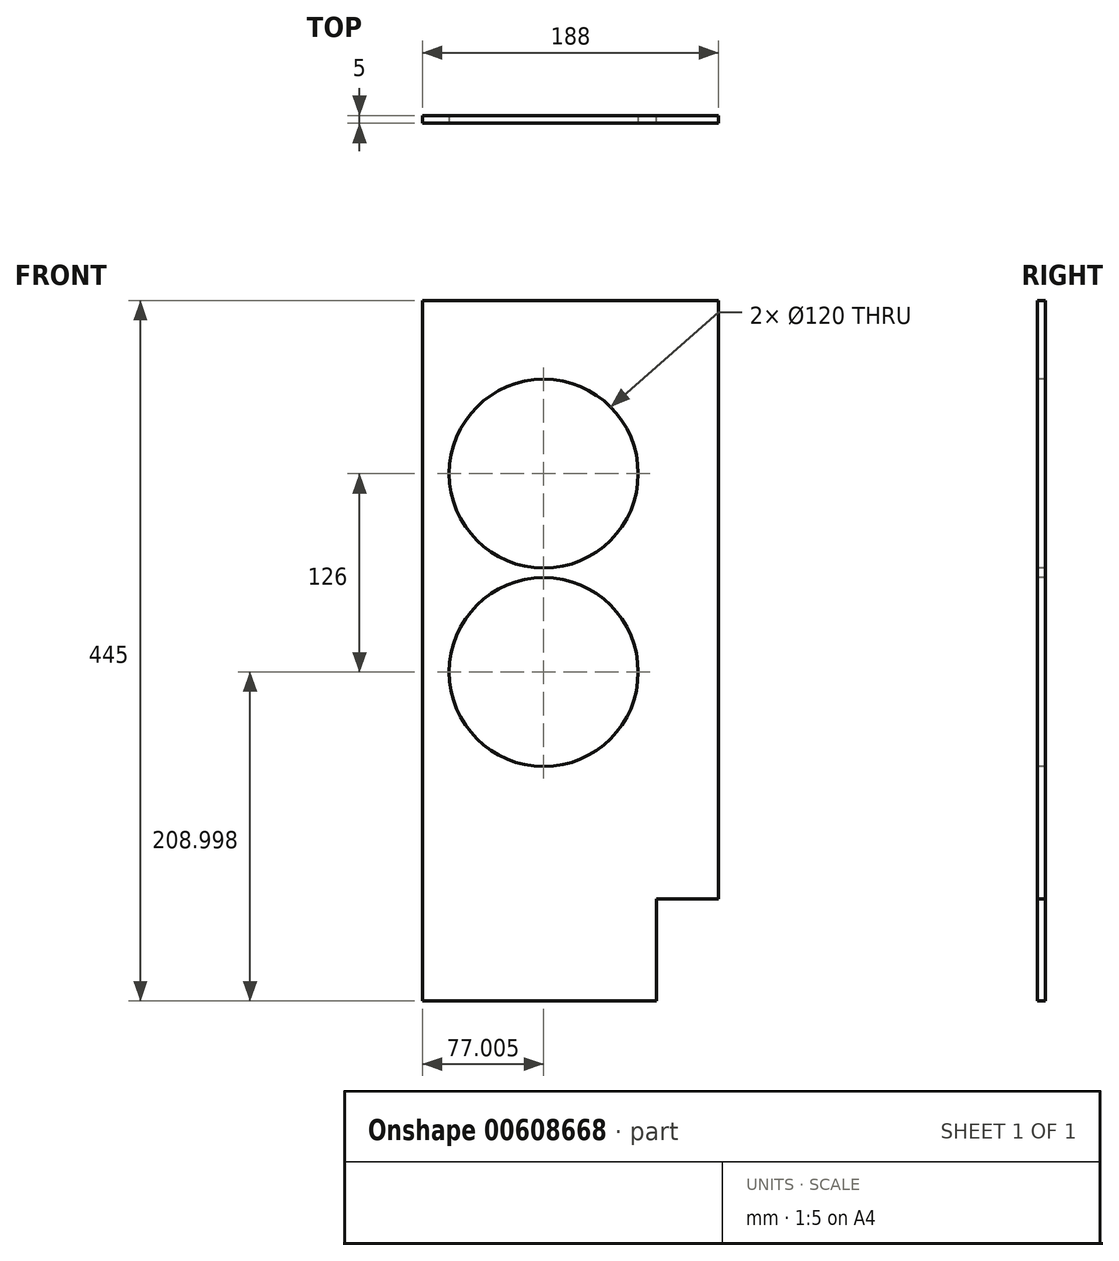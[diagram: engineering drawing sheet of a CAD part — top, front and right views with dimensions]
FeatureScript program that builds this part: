
annotation { "Feature Type Name" : "Feature", "Feature Type Description" : "" }
export const myFeature = defineFeature(function(context is Context, id is Id, definition is map)
    precondition{}
    {
        {
            var Q0;
            Q0=qCreatedBy(makeId("Front.planeOp"),FACE);
            var sketch = newSketch(context, id + "F0", { "sketchPlane" : qUnion([Q0])});
            skLineSegment(sketch, "E0.bottom", {"start": v(-455.9, 257.26) * mm, "end": v(-267.9, 257.26) * mm});
            skLineSegment(sketch, "E0.top", {"start": v(-455.9, -187.74) * mm, "end": v(-267.9, -187.74) * mm});
            skLineSegment(sketch, "E0.right", {"start": v(-267.9, 257.26) * mm, "end": v(-267.9, -187.74) * mm});
            skLineSegment(sketch, "E1.top", {"start": v(-307.4, -122.74) * mm, "end": v(-267.9, -122.74) * mm});
            skLineSegment(sketch, "E1.left", {"start": v(-307.4, -187.74) * mm, "end": v(-307.4, -122.74) * mm});
            skLineSegment(sketch, "E2", {"start": v(-455.9, -187.74) * mm, "end": v(-455.9, 257.26) * mm});
            skSolve(sketch);
        }
        {
            var Q0;
            Q0=makeQuery(id+"F0.imprint","IMPRINT",FACE,{"disambiguationData":[TD([[makeQuery(id+"F0.imprint","IMPRINT",EDGE,{"derivedFrom":sQuery(id+"F0.wireOp",EDGE,"E0.bottom")}),-1.0]])]});
            extrude(context, id + "F1", {"entities" : qUnion([Q0]), "depth" : 5 * mm, "offsetDistance" : 25 * mm});
        }
        {
            var Q0;
            Q0=makeQuery(id+"F1.opExtrude","CAP_FACE",FACE,{"disambiguationData":[OSD([sQuery(id+"F0.wireOp",EDGE,"E0.bottom"),sQuery(id+"F0.wireOp",EDGE,"E0.top"),sQuery(id+"F0.wireOp",EDGE,"E0.right"),sQuery(id+"F0.wireOp",EDGE,"E1.top"),sQuery(id+"F0.wireOp",EDGE,"E1.left"),sQuery(id+"F0.wireOp",EDGE,"E2")])],"isStart":false});
            var sketch = newSketch(context, id + "F2", { "sketchPlane" : qUnion([Q0])});
            skLineSegment(sketch, "E3.bottom", {"start": v(-455.9, 257.26) * mm, "end": v(-267.9, 257.26) * mm});
            skLineSegment(sketch, "E3.top", {"start": v(-455.9, 207.26) * mm, "end": v(-267.9, 207.26) * mm});
            skLineSegment(sketch, "E3.left", {"start": v(-455.9, 257.26) * mm, "end": v(-455.9, 207.26) * mm});
            skLineSegment(sketch, "E3.right", {"start": v(-267.9, 257.26) * mm, "end": v(-267.9, 207.26) * mm});
            skLineSegment(sketch, "E4.bottom", {"start": v(-455.9, 207.26) * mm, "end": v(-438.9, 207.26) * mm});
            skLineSegment(sketch, "E4.top", {"start": v(-455.9, -187.74) * mm, "end": v(-438.9, -187.74) * mm});
            skLineSegment(sketch, "E4.left", {"start": v(-455.9, 207.26) * mm, "end": v(-455.9, -187.74) * mm});
            skLineSegment(sketch, "E4.right", {"start": v(-438.9, 207.26) * mm, "end": v(-438.9, -187.74) * mm});
            skLineSegment(sketch, "E5.bottom", {"start": v(-438.9, 207.26) * mm, "end": v(-378.9, 207.26) * mm});
            skLineSegment(sketch, "E5.top", {"start": v(-438.9, 147.26) * mm, "end": v(-378.9, 147.26) * mm});
            skLineSegment(sketch, "E5.left", {"start": v(-438.9, 207.26) * mm, "end": v(-438.9, 147.26) * mm});
            skLineSegment(sketch, "E5.right", {"start": v(-378.9, 207.26) * mm, "end": v(-378.9, 147.26) * mm});
            skCircle(sketch, "E6", {"center": v(-378.9, 147.26) * mm, "radius": 60 * mm});
            skLineSegment(sketch, "E7", {"start": v(-378.9, 147.26) * mm, "end": v(-378.9, 87.26) * mm});
            skLineSegment(sketch, "E8", {"start": v(-378.9, 87.26) * mm, "end": v(-378.9, 81.26) * mm});
            skLineSegment(sketch, "E9", {"start": v(-378.9, 81.26) * mm, "end": v(-378.9, 21.26) * mm});
            skCircle(sketch, "E10", {"center": v(-378.9, 21.26) * mm, "radius": 60 * mm});
            skSolve(sketch);
        }
        {
            var Q0;
            {var subQ0=sQuery(id+"F2.wireOp",EDGE,"E10");var subQ1=makeQuery(id+"F2.imprint","INTERSECT",VERTEX,{"derivedFrom":[sQuery(id+"F2.wireOp",EDGE,"E8"),subQ0]});Q0=makeQuery(id+"F2.imprint","IMPRINT",FACE,{"disambiguationData":[TD([[makeQuery(id+"F2.imprint","IMPRINT",EDGE,{"disambiguationData":[TD([[subQ1,-1.0]])],"derivedFrom":subQ0}),1.0]])]});}
            var Q1;
            {var subQ0=sQuery(id+"F2.wireOp",EDGE,"E5.right");Q1=makeQuery(id+"F2.imprint","IMPRINT",FACE,{"disambiguationData":[TD([[makeQuery(id+"F2.imprint","IMPRINT",EDGE,{"derivedFrom":subQ0}),1.0]])]});}
            var Q2;
            {var subQ0=sQuery(id+"F2.wireOp",EDGE,"E5.top");Q2=makeQuery(id+"F2.imprint","IMPRINT",FACE,{"disambiguationData":[TD([[makeQuery(id+"F2.imprint","IMPRINT",EDGE,{"derivedFrom":subQ0}),-1.0]])]});}
            var Q3;
            {var subQ0=sQuery(id+"F2.wireOp",EDGE,"E5.top");Q3=makeQuery(id+"F2.imprint","IMPRINT",FACE,{"disambiguationData":[TD([[makeQuery(id+"F2.imprint","IMPRINT",EDGE,{"derivedFrom":subQ0}),1.0]])]});}
            extrude(context, id + "F3", {"entities" : qUnion([Q0, Q1, Q2, Q3]), "operationType" : NewBodyOperationType.REMOVE, "endBound" : BoundingType.THROUGH_ALL, "oppositeDirection" : true, "depth" : 25 * mm, "offsetDistance" : 25 * mm});
        }
    });
